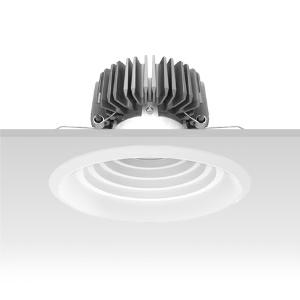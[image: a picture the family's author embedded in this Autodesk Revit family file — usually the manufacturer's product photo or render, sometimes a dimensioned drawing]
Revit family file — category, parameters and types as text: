
# Revit family: 3f_filippi_-_3f_reno_bianco_ampio_3f_filippi_-_30683_-_3f_reno_200_wh_3000-930_dali_wide
name_source: partatom
category: Lighting Fixtures
units: mm (PartAtom-declared; Revit-internal decimal feet)

## family parameters
Cut with Voids When Loaded = No
Host = Face
Light Source = No
Part Type = Normal
Room Calculation Point = No
Round Connector Dimension = Use Diameter
Shared = No

## types (1)
- 3F Filippi - 3F Reno Bianco Ampio (1 x LED, 2644 lm, 37 W, 3000 K)
    Apparent Load = 37 VA
    Approval mark = CE
    CIE Flux Codes = 80 97 100 100 100
    Color Rendering = 90
    Color Temperature = 3000 K
    Control Gear = Electronic transformer
    Default Elevation = 1800 mm
    Description = ILLUMINOTECHNICAL
Luminous efficiency 100% (DLOR 100%, ULOR 0%).
Initial luminous flux of the luminaire 2644 lm.
Direct symmetric wide distribution.
Installation Interdistance Transv.D = 1.56 x hu - Long.D = 1.56 x hu.
Tabular UGR (CIE 117 - 4H-8H; S=0.25H; 70/50/20): RUG 20.4 - 20.4.
Beam angle: 85° - 84°.
Luminous efficacy 71 lm/W.
Lifetime (L90/B10): 30000 h. (tq+25°C)
Lifetime (L85/B10): 50000 h. (tq+25°C)
Lifetime (L70/B10): 80000 h. (tq+25°C)
Sudden decreased luminous flux after 50000 hours: 0% (C0).
Photobiological safety in compliance with IEC/TR 62778: RG0 risk exempt, (IEC 62471).
In compliance with IEC/EN 62722-2-1 - IEC/EN 62717 standards.

SOURCE
Compact LED module 3000/930.
Energy efficiency class (UE 2019/2020 - UE 2019/2015): E.
CIE 13.3 Colour rendering index: CRI >90 (R9 >50%).
IES TM-30 Fidelity Index: Rf = 92 Rg = 101.
CCT nominal colour temperature 3000 K.
Colour initial tolerance (MacAdam): SDCM 3.
Zhaga Book 3 compliant.

MECHANICAL
Passive heat dissipator in die-casting aluminium, oversized, for optimum thermal management of the LED module.
Parabolic element with graduated/concentric rings in white polycarbonate.
Transparent external lens with glossy and satin differentiated surfaces, with a cooling and anti-insect system in methacrylate (PMMA).
Fastening spring clips in stainless steel.
Dimensions: diameter 216 mm, height 142 mm. Weight 1.495 kg.
IP44 protection degree for exposed part, IP20 for recessed part.
Mechanical strength to impacts IK04 (0.5 joule).
Glow-wire test resistance 650°C.

ELECTRICAL
Wiring on a separate unit.
Halogen Free DALI-2 DATI (Parts 251, 252, 253), PUSH-DIM, electronic wiring 230V-50/60Hz, power factor 0.97 at full load, THD <25%, constant output current, SELV, class II, 1 driver, 1 DALI addresse.
Power of the luminaire 37 W.
ENEC - CE.
SAFE FLICKER: PstLM=<1 and SVM=<0.4 (IEC TR 61547-1 and IEC TR 63158), to ensure a more comfortable and safe light.
Luminaire compliant with EN 60598-2-22 for power supply from a centralised emergency system CPSS (Central Power Supply System), not incorporated in the luminaire - high risk areas excluded. The default power and flux are 100% in AC and 100% in DC.
Ambient temperature from 0°C to +25°C.
Temperature class T6 max 85°C.
Relative humidity UR: <85%.

INSTALLATION
Pull-up recessed fitting.
False ceiling carving: 200 mm.
All accessories dedicated to this product are available on the Catalog and on our website www.3F-Filippi.com.

APPLICATIONS
Environments: architectural, commercial, exhibition areas, transit areas, corridors, shops, display windows, service areas.
In false ceilings with narrow voids.

LIGHT MANAGEMENT
Recommended minimum setting: 10%.
The luminaire, equipped with (DALI-2 DATI) driver, can be controlled manually with 3F Easy Dim technology or automatically/manually with wired or wireless DALI/D2D control systems.
The D2D driver guarantees interoperability with other devices with the same certification by making the following information available:
Device Data (Part 251), Energy Report (Part 252), Diagnosis & Maintenance (Part 253).
In electrical systems without a regulation system (manual or automatic) and DALI bus, a suitable jumper must be made on the DA-DA terminals of the appliance.

WARNING
Luminaire designed for disposal/recycling at end-of-life.
Replaceable (LED only) light source by a professional. Replaceable control gear by a professional.
    Height = 0 mm  [stored 0 ft]
    Lamp = 1 x LED
    Lamp Light Flux = 2644 lm
    Lamp Power = 37 W
    Lamp count = 1
    Length = 216 mm
    Lifetime = 50000 h
    Luminous efficacy = 71 lm/W
    Manufacturer = 3F Filippi
    ModVariant = No
    Model = 3F Filippi - 30683 - 3F Reno 200 WH 3000-930 DALI WIDE
    Mounting Place = Ceiling
    Mounting Type = Recessed
    Number of Poles = 1
    OnlyDefault = Yes
    Power Factor = 1
    Product Name = 3F Filippi - 3F Reno Bianco Ampio
    Product group = recessed luminaire
    ProductGroupID = 4
    Protection Class = Protection class II
    Protection Degree = IP 20
    RLX_Detail_Level = 1
    RLX_Emergency_Light_Flux = 0 lm
    RLX_Emergency_Type = 0
    RLX_Emergency_Type_DB = No
    RlxData = <blob elided: 94173 chars, md5=1a0d9c88>
    Socket = socket
    Standby Power = 0 W
    System Light Flux = 2644 lm
    System Power = 37 W
    Type Comments = Product without accessories
    Type Image = 3ffilippi_3f_reno_200_wh_2500_3000_4000.jpg
    URL = http://relux.com
    VarID = ---
    Voltage = 0 V
    Weight = 0.00 kg
    Width = 0 mm  [stored 0 ft]

note: [stored X ft] marks values corroborated as IEEE doubles in the binary element streams (Revit-internal decimal feet)

## geometry (parser evidence)
native form markers: Blend x4, Sweep x11
no freeform markers — native parametric forms only
